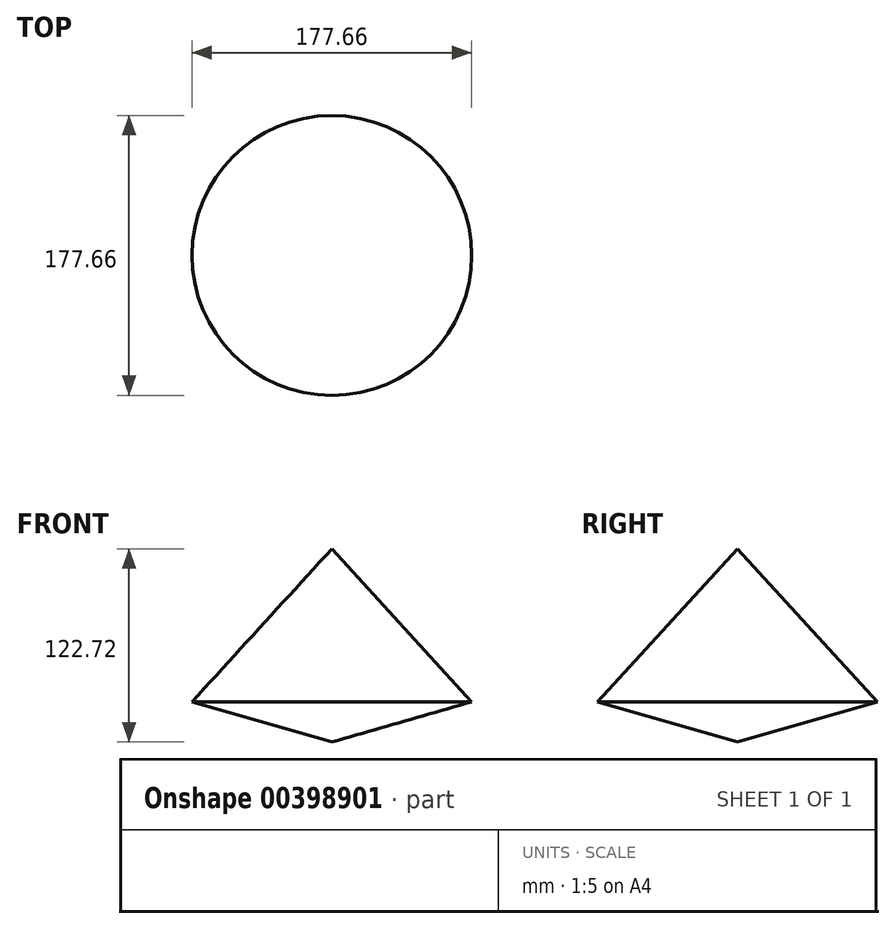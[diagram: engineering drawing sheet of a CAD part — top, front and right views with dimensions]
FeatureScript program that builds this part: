
annotation { "Feature Type Name" : "Feature", "Feature Type Description" : "" }
export const myFeature = defineFeature(function(context is Context, id is Id, definition is map)
    precondition{}
    {
        {
            var Q0;
            Q0=qCreatedBy(makeId("Front.planeOp"),FACE);
            var sketch = newSketch(context, id + "F0", { "sketchPlane" : qUnion([Q0])});
            skLineSegment(sketch, "E0", {"start": v(0, 74.27) * mm, "end": v(0, -48.45) * mm});
            skLineSegment(sketch, "E1", {"start": v(0, 74.27) * mm, "end": v(88.83, -23) * mm});
            skLineSegment(sketch, "E2", {"start": v(88.83, -23) * mm, "end": v(0, -48.45) * mm});
            skSolve(sketch);
        }
        {
            var Q0;
            Q0=makeQuery(id+"F0.imprint","IMPRINT",FACE,{"disambiguationData":[TD([[makeQuery(id+"F0.imprint","IMPRINT",EDGE,{"derivedFrom":sQuery(id+"F0.wireOp",EDGE,"E0")}),1.0]])]});
            var Q1;
            Q1=sQuery(id+"F0.wireOp",EDGE,"E0");
            revolve(context, id + "F1", {"entities" : qUnion([Q0]), "axis" : qUnion([Q1]), "revolveType" : RevolveType.FULL});
        }
    });
